# Revit family: Toilet_Tank-American_Standard-Cadet-4188A.104
name_source: partatom
category: Plumbing Fixtures
units: mm (PartAtom-declared; Revit-internal decimal feet)

## family parameters
Always vertical = No
Cut with Voids When Loaded = No
Part Type = Normal
Room Calculation Point = No
Round Connector Dimension = Use Diameter
Shared = Yes
Work Plane-Based = Yes

## types (1)
- Must Match "Model" Value
    CW Connection = No
    Cold Water Connection Diameter = 0"
    Cold Water Connection Height = 0"
    Cold Water Connection Radius = 0"
    Default Elevation = 0"
    HW Connection = No
    Height = 0"
    Hot Water Connection Diameter = 0"
    Hot Water Connection Height = 0"
    Hot Water Connection Radius = 0"
    Is ADA Compliant = No
    Length = 0"
    Material = Default
    Price = Prices may vary. Please consult Manufacturer Representative for most up-to-date price list.
    Vent Connection = No
    Waste Connection = No
    Waste Connection Diameter = 0"
    Waste Connection Height = 0"
    Waste Connection Radius = 0"
    Width = 0"

## geometry (parser evidence)
native form markers: Sweep x2
no freeform markers — native parametric forms only
